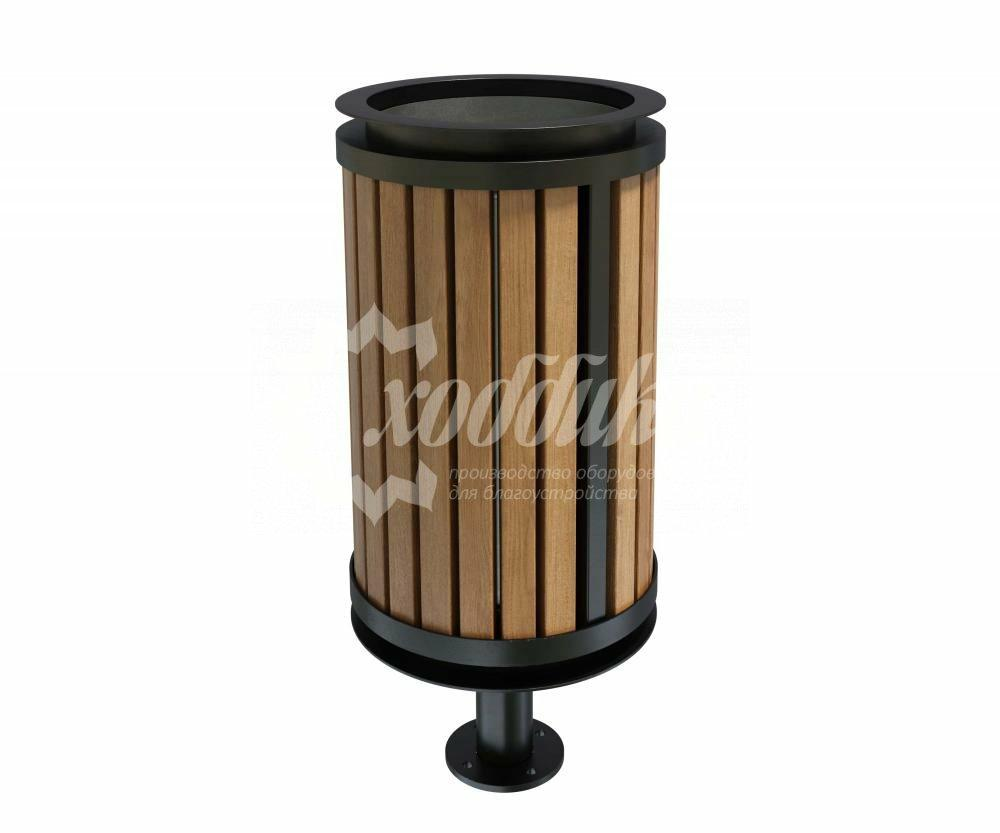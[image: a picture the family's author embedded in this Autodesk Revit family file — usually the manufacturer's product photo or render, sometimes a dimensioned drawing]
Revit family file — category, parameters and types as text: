
# Revit family: Урна уличная «Радиус-3» Арт 12225
name_source: partatom
category: Антураж
revit_build: Autodesk Revit 2018 (Build: 20180423_1000(x64)
units: mm (PartAtom-declared; Revit-internal decimal feet)

## family parameters
Всегда вертикально = Да
Источник визуального образа = Геометрия семейства
На основе рабочей плоскости = Нет
Общий = Нет
При загрузке вырезать с полостями = Нет
Точка расчета площади = Нет

## types (2) — shared parameters
URL = https://hobbyka.ru
Артикул товара = Арт. 12225
Высота = 894 мм
Группа модели = Уличные урны
Диаметр = 400 мм
Длина = 400 мм
Изготовитель = ООО «Хоббика»
Изображение типоразмера = Урна уличная «Радиус-3» Арт 12225.jpg
Материал изделия = Сталь, дерево
Цвет каркаса = Сталь
Ширина = 400 мм

## per-type parameters (varying)
| type | Версия "Ангарская сосна" | Версия "Лиственница" | Цвет отделки |
| Урна уличная «Радиус-3». Версия Ангарская сосна | Да | Нет | Сосна |
| Урна уличная «Радиус-3». Версия Лиственница | Нет | Да | Лиственница |

note: column(s) folded — value = type name in every type: Описание
